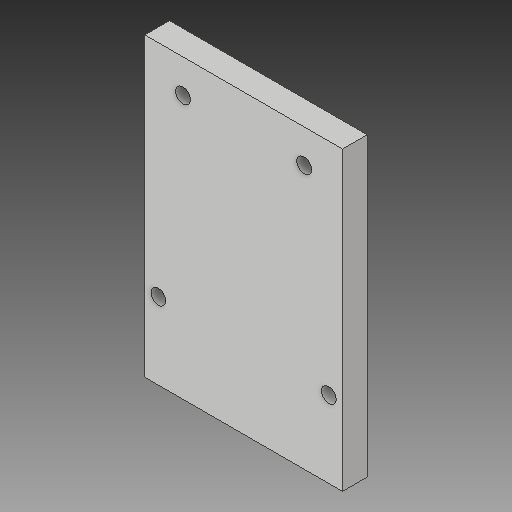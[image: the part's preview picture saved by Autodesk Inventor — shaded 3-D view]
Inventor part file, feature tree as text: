
AUTODESK INVENTOR PART (.ipt)
format: ipt  version: 2018 (Build 220112000, 112)  size: 115,712 bytes
history: native  units: in
note: dims shown in document units (in); Inventor stores cm internally (conversion verified against a paired STEP export)
features: extrude x2, sketch x2
ambient origin geometry x8: Origin, YZ Plane, XZ Plane, XY Plane, X Axis, Y Axis, Z Axis, Center Point
bodies: Solid1 (feature_tree)
feature tree (4):
  extrude  "Extrusion1"  Depth=2.3622in
  extrude  "Extrusion2"  Depth=0.1969in
  sketch  "Sketch1"  dims[d0=1.5748in d1=2.3622in]
  sketch  "Sketch2"  dims[d2=0.1969in d3=0.0in d4=0.6102in d5=0.1181in d6=0.1181in d9=0.2657in d12=0.1181in d13=0.1181in d14=1.0in d15=0.0in d16=1.3583in d17=0.6791in d18=0.6791in d19=0.9646in d20=0.4823in d21=0.4823in]
